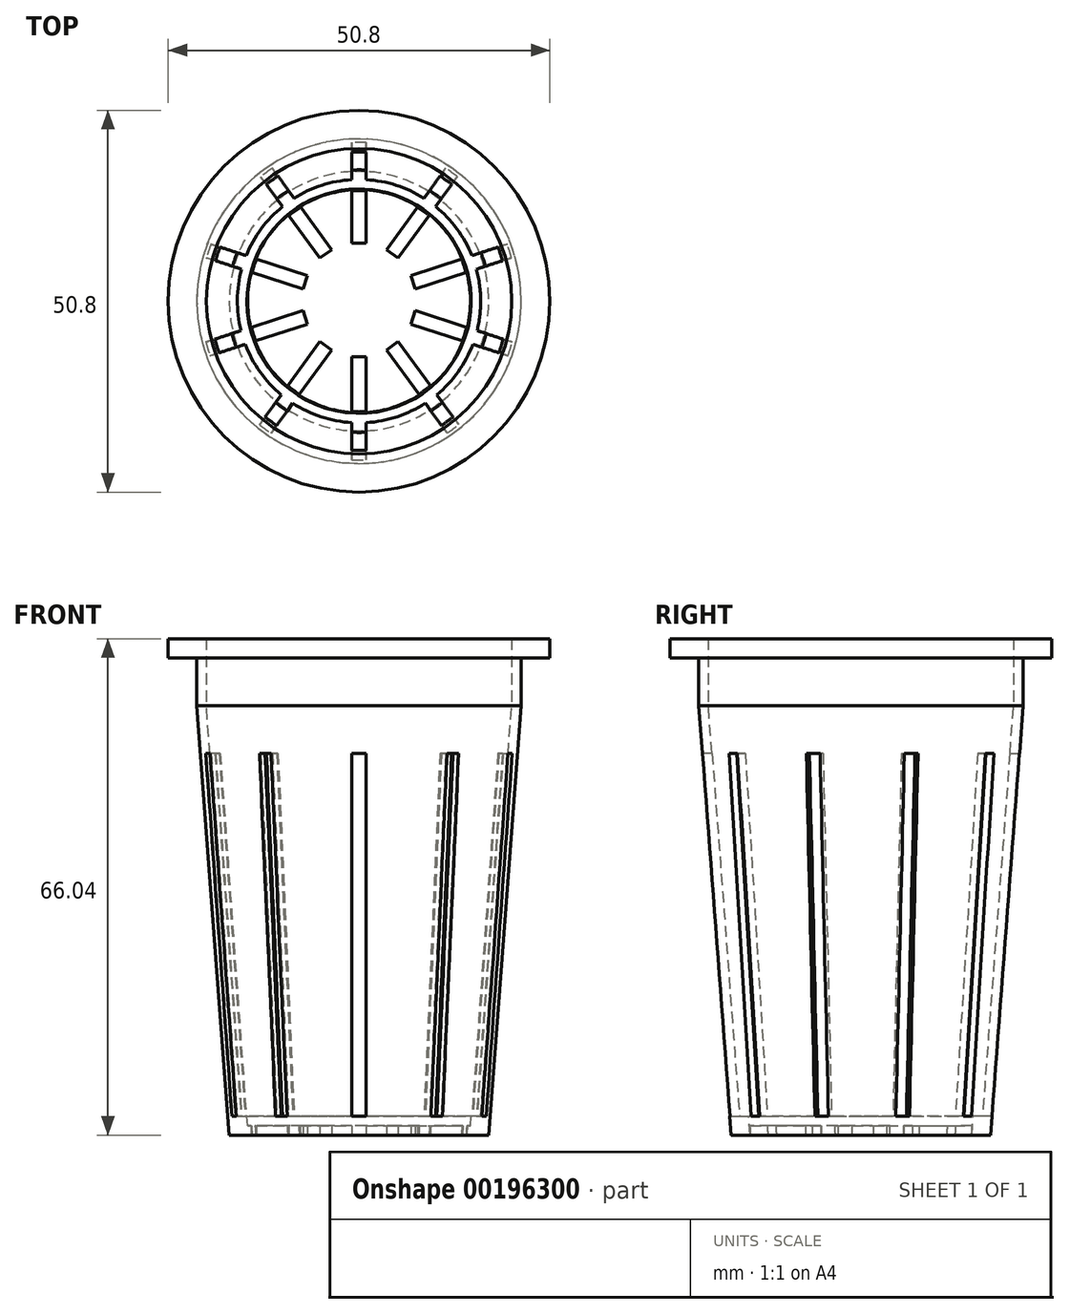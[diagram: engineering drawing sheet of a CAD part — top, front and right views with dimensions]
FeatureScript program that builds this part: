
annotation { "Feature Type Name" : "Feature", "Feature Type Description" : "" }
export const myFeature = defineFeature(function(context is Context, id is Id, definition is map)
    precondition{}
    {
        {
            var Q0;
            Q0=qCreatedBy(makeId("Front.planeOp"),FACE);
            var sketch = newSketch(context, id + "F0", { "sketchPlane" : qUnion([Q0])});
            skLineSegment(sketch, "E0", {"start": v(0, 0) * mm, "end": v(0, 63.5) * mm});
            skLineSegment(sketch, "E1", {"start": v(0, 63.5) * mm, "end": v(0, 66.04) * mm});
            skLineSegment(sketch, "E2", {"start": v(0, 66.04) * mm, "end": v(25.4, 66.04) * mm});
            skLineSegment(sketch, "E3", {"start": v(25.4, 66.04) * mm, "end": v(25.4, 63.5) * mm});
            skLineSegment(sketch, "E4", {"start": v(25.4, 63.5) * mm, "end": v(0, 63.5) * mm});
            skLineSegment(sketch, "E5", {"start": v(0, 63.5) * mm, "end": v(21.59, 63.5) * mm});
            skLineSegment(sketch, "E6", {"start": v(0, 0) * mm, "end": v(17.27, 0) * mm});
            skLineSegment(sketch, "E7", {"start": v(21.59, 63.5) * mm, "end": v(21.59, 57.15) * mm});
            skLineSegment(sketch, "E8", {"start": v(21.6, 57.15) * mm, "end": v(17.27, 0) * mm});
            skLineSegment(sketch, "E9", {"start": v(0, 0) * mm, "end": v(0, 2.54) * mm});
            skLineSegment(sketch, "E10", {"start": v(0, 2.54) * mm, "end": v(17.46, 2.54) * mm});
            skSolve(sketch);
        }
        {
            var Q0;
            Q0 = qSketchRegion(id + "F0", true);
            var Q1;
            Q1=sQuery(id+"F0.wireOp",EDGE,"E0");
            revolve(context, id + "F1", {"entities" : qUnion([Q0]), "axis" : qUnion([Q1]), "revolveType" : RevolveType.FULL});
        }
        {
            var Q0;
            Q0=makeQuery(id+"F1.opRevolve","SWEPT_FACE",FACE,{"disambiguationData":[OSD([sQuery(id+"F0.wireOp",EDGE,"E2")])]});
            shell(context, id + "F2", {"entities" : qUnion([Q0]), "thickness" : 1.27 * mm});
        }
        {
            var Q0;
            Q0=makeQuery(id+"F2.opShell","OFFSET_FACE",FACE,{"disambiguationData":[OSD([sQuery(id+"F0.wireOp",EDGE,"E4")])]});
            extrude(context, id + "F3", {"entities" : qUnion([Q0]), "operationType" : NewBodyOperationType.ADD, "depth" : 1.27 * mm});
        }
        {
            var Q0;
            Q0=qCreatedBy(makeId("Top.planeOp"),FACE);
            cPlane(context, id + "F4", {"entities" : qUnion([Q0]), "cplaneType" : CPlaneType.OFFSET, "offset" : 63.5 * mm, "width" : 152.4 * mm, "height" : 152.4 * mm});
        }
        {
            var Q0;
            Q0=qCreatedBy(id+"F4.planeOp",FACE);
            var sketch = newSketch(context, id + "F5", { "sketchPlane" : qUnion([Q0])});
            skCircle(sketch, "E11", {"center": v(0, 0) * mm, "radius": 20.32 * mm});
            skSolve(sketch);
        }
        {
            var Q0;
            Q0 = qSketchRegion(id + "F5", true);
            extrude(context, id + "F6", {"entities" : qUnion([Q0]), "operationType" : NewBodyOperationType.REMOVE, "depth" : 25.4 * mm});
        }
        {
            var Q0;
            Q0=qCreatedBy(makeId("Top.planeOp"),FACE);
            var sketch = newSketch(context, id + "F7", { "sketchPlane" : qUnion([Q0])});
            skLineSegment(sketch, "E12", {"start": v(0, 0) * mm, "end": v(0, -17.27) * mm});
            skLineSegment(sketch, "E13.bottom", {"start": v(0.95, -7.37) * mm, "end": v(-0.95, -7.37) * mm});
            skLineSegment(sketch, "E13.top", {"start": v(0.95, -27.18) * mm, "end": v(-0.95, -27.18) * mm});
            skLineSegment(sketch, "E13.left", {"start": v(0.95, -7.37) * mm, "end": v(0.95, -27.18) * mm});
            skLineSegment(sketch, "E13.right", {"start": v(-0.95, -7.37) * mm, "end": v(-0.95, -27.18) * mm});
            skPoint(sketch, "E13.middle", {"position": v(0, -17.27) * mm});
            skLineSegment(sketch, "E14.1.0", {"start": v(3.67, -6.48) * mm, "end": v(15.31, -22.51) * mm});
            skLineSegment(sketch, "E14.1.1", {"start": v(5.2, -5.36) * mm, "end": v(16.85, -21.4) * mm});
            skLineSegment(sketch, "E14.1.2", {"start": v(5.2, -5.36) * mm, "end": v(3.67, -6.48) * mm});
            skLineSegment(sketch, "E14.1.3", {"start": v(16.85, -21.4) * mm, "end": v(15.31, -22.51) * mm});
            skLineSegment(sketch, "E14.2.0", {"start": v(6.88, -3.06) * mm, "end": v(25.73, -9.18) * mm});
            skLineSegment(sketch, "E14.2.1", {"start": v(7.47, -1.24) * mm, "end": v(26.31, -7.37) * mm});
            skLineSegment(sketch, "E14.2.2", {"start": v(7.47, -1.24) * mm, "end": v(6.88, -3.06) * mm});
            skLineSegment(sketch, "E14.2.3", {"start": v(26.31, -7.37) * mm, "end": v(25.73, -9.18) * mm});
            skLineSegment(sketch, "E14.3.0", {"start": v(7.47, 1.6) * mm, "end": v(26.31, 7.73) * mm});
            skLineSegment(sketch, "E14.3.1", {"start": v(6.88, 3.42) * mm, "end": v(25.73, 9.54) * mm});
            skLineSegment(sketch, "E14.3.2", {"start": v(6.88, 3.42) * mm, "end": v(7.47, 1.6) * mm});
            skLineSegment(sketch, "E14.3.3", {"start": v(25.73, 9.54) * mm, "end": v(26.31, 7.73) * mm});
            skLineSegment(sketch, "E14.4.0", {"start": v(5.2, 5.73) * mm, "end": v(16.85, 21.76) * mm});
            skLineSegment(sketch, "E14.4.1", {"start": v(3.67, 6.85) * mm, "end": v(15.31, 22.88) * mm});
            skLineSegment(sketch, "E14.4.2", {"start": v(3.67, 6.85) * mm, "end": v(5.2, 5.73) * mm});
            skLineSegment(sketch, "E14.4.3", {"start": v(15.31, 22.88) * mm, "end": v(16.85, 21.76) * mm});
            skLineSegment(sketch, "E14.5.0", {"start": v(0.95, 7.73) * mm, "end": v(0.95, 27.54) * mm});
            skLineSegment(sketch, "E14.5.1", {"start": v(-0.95, 7.73) * mm, "end": v(-0.95, 27.54) * mm});
            skLineSegment(sketch, "E14.5.2", {"start": v(-0.95, 7.73) * mm, "end": v(0.95, 7.73) * mm});
            skLineSegment(sketch, "E14.5.3", {"start": v(-0.95, 27.54) * mm, "end": v(0.95, 27.54) * mm});
            skLineSegment(sketch, "E14.6.0", {"start": v(-3.67, 6.85) * mm, "end": v(-15.31, 22.88) * mm});
            skLineSegment(sketch, "E14.6.1", {"start": v(-5.2, 5.73) * mm, "end": v(-16.85, 21.76) * mm});
            skLineSegment(sketch, "E14.6.2", {"start": v(-5.2, 5.73) * mm, "end": v(-3.67, 6.85) * mm});
            skLineSegment(sketch, "E14.6.3", {"start": v(-16.85, 21.76) * mm, "end": v(-15.31, 22.88) * mm});
            skLineSegment(sketch, "E14.7.0", {"start": v(-6.88, 3.42) * mm, "end": v(-25.73, 9.54) * mm});
            skLineSegment(sketch, "E14.7.1", {"start": v(-7.47, 1.6) * mm, "end": v(-26.31, 7.73) * mm});
            skLineSegment(sketch, "E14.7.2", {"start": v(-7.47, 1.6) * mm, "end": v(-6.88, 3.42) * mm});
            skLineSegment(sketch, "E14.7.3", {"start": v(-26.31, 7.73) * mm, "end": v(-25.73, 9.54) * mm});
            skLineSegment(sketch, "E14.8.0", {"start": v(-7.47, -1.24) * mm, "end": v(-26.31, -7.37) * mm});
            skLineSegment(sketch, "E14.8.1", {"start": v(-6.88, -3.06) * mm, "end": v(-25.73, -9.18) * mm});
            skLineSegment(sketch, "E14.8.2", {"start": v(-6.88, -3.06) * mm, "end": v(-7.47, -1.24) * mm});
            skLineSegment(sketch, "E14.8.3", {"start": v(-25.73, -9.18) * mm, "end": v(-26.31, -7.37) * mm});
            skLineSegment(sketch, "E14.9.0", {"start": v(-5.2, -5.36) * mm, "end": v(-16.85, -21.4) * mm});
            skLineSegment(sketch, "E14.9.1", {"start": v(-3.67, -6.48) * mm, "end": v(-15.31, -22.51) * mm});
            skLineSegment(sketch, "E14.9.2", {"start": v(-3.67, -6.48) * mm, "end": v(-5.2, -5.36) * mm});
            skLineSegment(sketch, "E14.9.3", {"start": v(-15.31, -22.51) * mm, "end": v(-16.85, -21.4) * mm});
            skPoint(sketch, "E14.center", {"position": v(0, 0.18) * mm});
            skSolve(sketch);
        }
        {
            var Q0;
            Q0 = qSketchRegion(id + "F7", true);
            extrude(context, id + "F8", {"entities" : qUnion([Q0]), "operationType" : NewBodyOperationType.REMOVE, "depth" : 50.8 * mm});
        }
        {
            var Q0;
            Q0=qCreatedBy(makeId("Front.planeOp"),FACE);
            var sketch = newSketch(context, id + "F9", { "sketchPlane" : qUnion([Q0])});
            skLineSegment(sketch, "E15", {"start": v(0, 0) * mm, "end": v(17.27, 0) * mm});
            skLineSegment(sketch, "E16", {"start": v(0, 0) * mm, "end": v(0, 2.54) * mm});
            skLineSegment(sketch, "E17", {"start": v(0, 2.54) * mm, "end": v(17.46, 2.54) * mm});
            skLineSegment(sketch, "E18", {"start": v(17.46, 2.54) * mm, "end": v(17.27, 0) * mm});
            skLineSegment(sketch, "E19", {"start": v(17.27, 0) * mm, "end": v(14.73, 0) * mm});
            skLineSegment(sketch, "E20", {"start": v(14.73, 0) * mm, "end": v(14.92, 2.54) * mm});
            skSolve(sketch);
        }
        {
            var Q0;
            {var subQ0=sQuery(id+"F9.wireOp",EDGE,"E18");Q0=makeQuery(id+"F9.imprint","IMPRINT",FACE,{"disambiguationData":[TD([[makeQuery(id+"F9.imprint","IMPRINT",EDGE,{"derivedFrom":subQ0}),-1.0]])]});}
            var Q1;
            Q1=sQuery(id+"F9.wireOp",EDGE,"E16");
            revolve(context, id + "F10", {"operationType" : NewBodyOperationType.ADD, "entities" : qUnion([Q0]), "axis" : qUnion([Q1]), "revolveType" : RevolveType.FULL});
        }
    });
